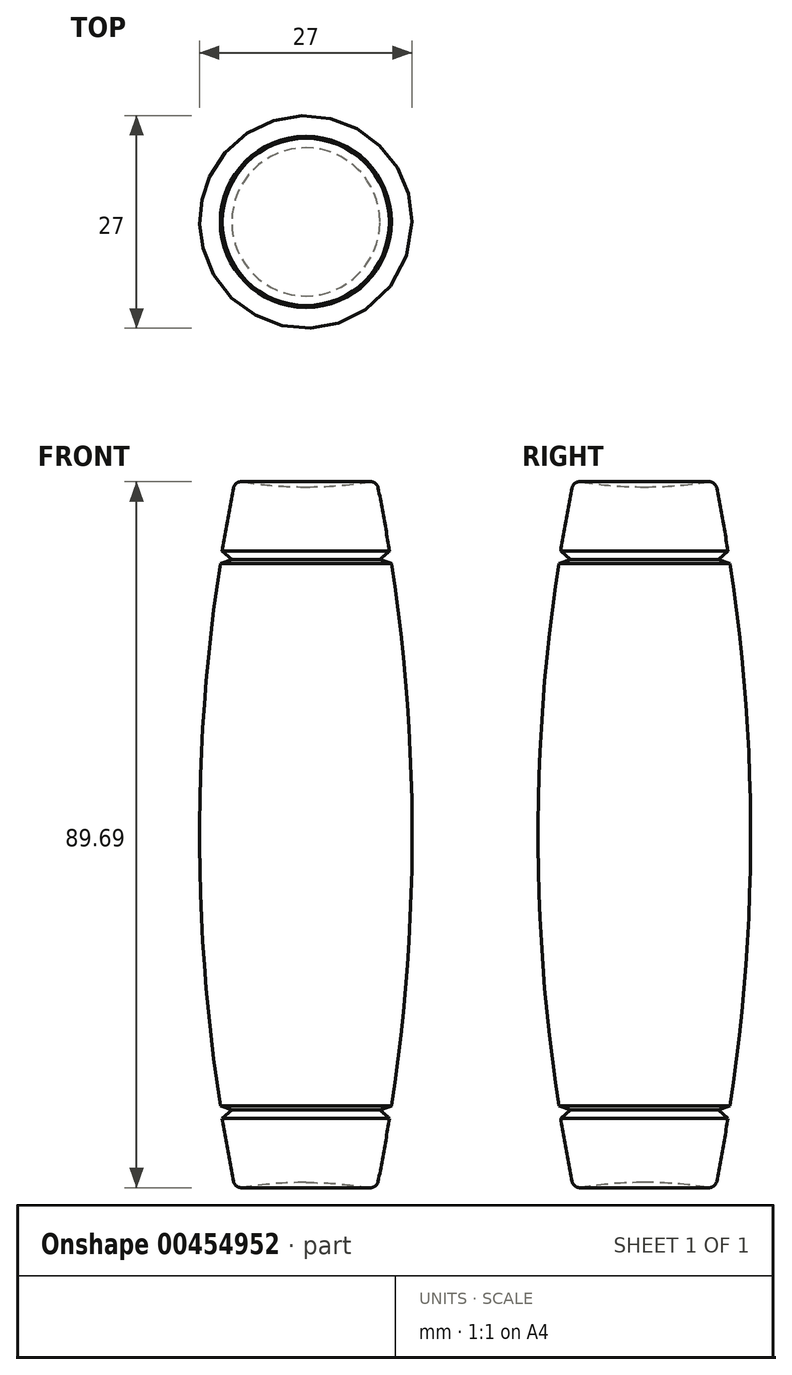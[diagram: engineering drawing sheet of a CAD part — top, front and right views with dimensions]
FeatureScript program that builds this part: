
annotation { "Feature Type Name" : "Feature", "Feature Type Description" : "" }
export const myFeature = defineFeature(function(context is Context, id is Id, definition is map)
    precondition{}
    {
        {
            var Q0;
            Q0=qCreatedBy(makeId("Front.planeOp"),FACE);
            var sketch = newSketch(context, id + "F0", { "sketchPlane" : qUnion([Q0])});
            skLineSegment(sketch, "E0", {"start": v(0, 0) * mm, "end": v(0, 88.37) * mm, "construction": true});
            skArc(sketch, "E1", {"start": v(9, -0.82) * mm, "mid": v(13.5, 44.18) * mm, "end": v(9, 89.18) * mm});
            skLineSegment(sketch, "E2", {"start": v(-213.5, 44.18) * mm, "end": v(0, 44.18) * mm, "construction": true});
            skLineSegment(sketch, "E3", {"start": v(13.5, 44.18) * mm, "end": v(13.5, 17.37) * mm, "construction": true});
            skLineSegment(sketch, "E4", {"start": v(0, 0) * mm, "end": v(0, 88.37) * mm});
            skArc(sketch, "E5", {"start": v(0, 88.37) * mm, "mid": v(4.52, 88.57) * mm, "end": v(9, 89.18) * mm});
            skLineSegment(sketch, "E6", {"start": v(9, 89.18) * mm, "end": v(-10.02, 89.18) * mm, "construction": true});
            skArc(sketch, "E7.MirrorCS", {"start": v(0, 0) * mm, "mid": v(4.52, -0.2) * mm, "end": v(9, -0.82) * mm});
            skLineSegment(sketch, "E8", {"start": v(9, -0.82) * mm, "end": v(-18, -0.82) * mm, "construction": true});
            skLineSegment(sketch, "E9", {"start": v(0, 88.37) * mm, "end": v(34.96, 88.37) * mm, "construction": true});
            skLineSegment(sketch, "E10", {"start": v(0, 0) * mm, "end": v(28.63, -0.2) * mm, "construction": true});
            skPoint(sketch, "E10.endSnap0", {"position": v(4.52, -0.2) * mm});
            skSolve(sketch);
        }
        {
            var Q0;
            Q0=makeQuery(id+"F0.imprint","IMPRINT",FACE,{"disambiguationData":[TD([[makeQuery(id+"F0.imprint","IMPRINT",EDGE,{"derivedFrom":sQuery(id+"F0.wireOp",EDGE,"E1")}),1.0]])]});
            var Q1;
            Q1=sQuery(id+"F0.wireOp",EDGE,"E4");
            revolve(context, id + "F1", {"entities" : qUnion([Q0]), "axis" : qUnion([Q1]), "revolveType" : RevolveType.FULL});
        }
        {
            var Q0;
            Q0=makeQuery(id+"F1.opRevolve","SWEPT_EDGE",EDGE,{"disambiguationData":[OSD([sQuery(id+"F0.wireOp",EDGE,"E1"),sQuery(id+"F0.wireOp",EDGE,"E5")])]});
            var Q1;
            Q1=makeQuery(id+"F1.opRevolve","SWEPT_EDGE",EDGE,{"disambiguationData":[OSD([sQuery(id+"F0.wireOp",EDGE,"E1"),sQuery(id+"F0.wireOp",EDGE,"E7.MirrorCS")])]});
            fillet(context, id + "F2", {"entities" : qUnion([Q0, Q1]), "radius" : 1 * mm, "tangentPropagation" : true, "allowEdgeOverflow" : false});
        }
        {
            var Q0;
            Q0=qCreatedBy(makeId("Front.planeOp"),FACE);
            var sketch = newSketch(context, id + "F3", { "sketchPlane" : qUnion([Q0])});
            skArc(sketch, "E11", {"start": v(-8.04, 89.02) * mm, "mid": v(0, 88.37) * mm, "end": v(8.04, 89.02) * mm, "construction": true});
            skArc(sketch, "E12", {"start": v(8.04, -0.65) * mm, "mid": v(0, 0) * mm, "end": v(-8.04, -0.65) * mm, "construction": true});
            skLineSegment(sketch, "E13", {"start": v(8.04, 89.02) * mm, "end": v(8.04, -0.65) * mm, "construction": true});
            skLineSegment(sketch, "E14", {"start": v(8.04, 44.18) * mm, "end": v(-31.5, 44.18) * mm, "construction": true});
            skLineSegment(sketch, "E15", {"start": v(14.73, 83.85) * mm, "end": v(9.4, 79.14) * mm});
            skLineSegment(sketch, "E16", {"start": v(9.4, 79.14) * mm, "end": v(17.61, 76.39) * mm});
            skLineSegment(sketch, "E17", {"start": v(14.73, 83.85) * mm, "end": v(17.61, 76.39) * mm});
            skLineSegment(sketch, "E18.MirrorCS", {"start": v(14.73, 4.52) * mm, "end": v(9.4, 9.23) * mm});
            skLineSegment(sketch, "E19.MirrorCS", {"start": v(9.4, 9.23) * mm, "end": v(17.61, 11.98) * mm});
            skLineSegment(sketch, "E20.MirrorCS", {"start": v(14.73, 4.52) * mm, "end": v(17.61, 11.98) * mm});
            skLineSegment(sketch, "E21", {"start": v(0, 0) * mm, "end": v(0, 55.62) * mm, "construction": true});
            skSolve(sketch);
        }
        {
            var Q0;
            Q0 = qSketchRegion(id + "F3", true);
            var Q1;
            Q1=sQuery(id+"F3.wireOp",EDGE,"E21");
            revolve(context, id + "F4", {"operationType" : NewBodyOperationType.REMOVE, "entities" : qUnion([Q0]), "axis" : qUnion([Q1]), "revolveType" : RevolveType.FULL, "oppositeDirection" : true});
        }
    });
